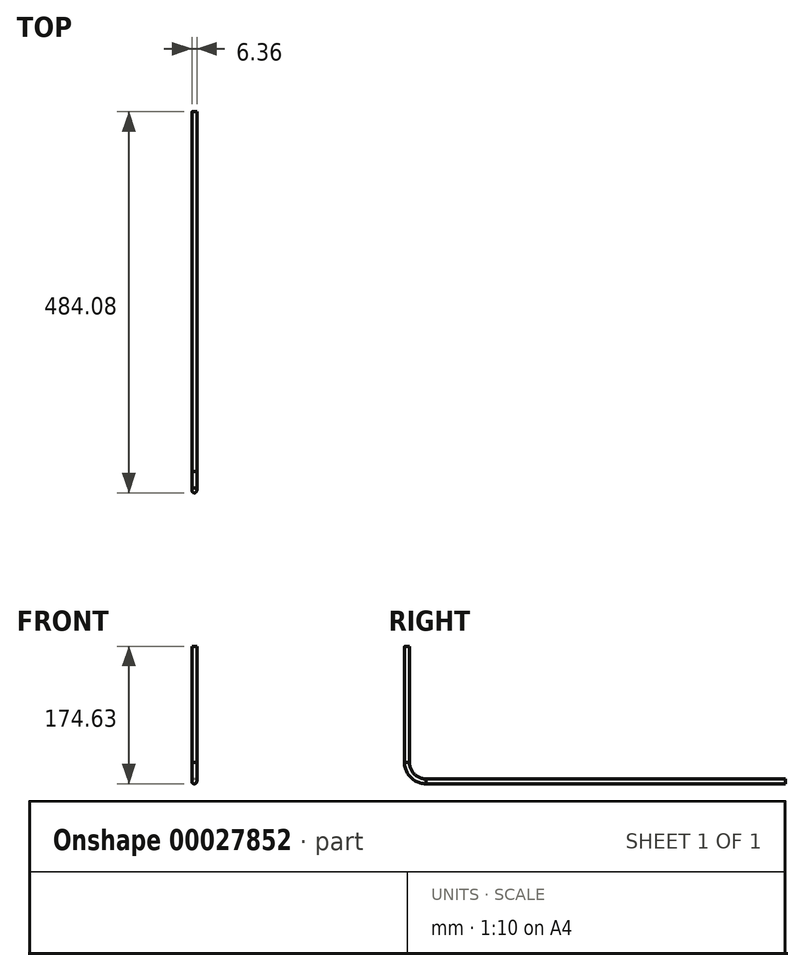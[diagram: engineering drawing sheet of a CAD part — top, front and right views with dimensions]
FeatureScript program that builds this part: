
annotation { "Feature Type Name" : "Feature", "Feature Type Description" : "" }
export const myFeature = defineFeature(function(context is Context, id is Id, definition is map)
    precondition{}
    {
        {
            var Q0;
            Q0=qCreatedBy(makeId("Top.planeOp"),FACE);
            var sketch = newSketch(context, id + "F0", { "sketchPlane" : qUnion([Q0])});
            skCircle(sketch, "E0", {"center": v(0, 0) * mm, "radius": 3.18 * mm});
            skSolve(sketch);
        }
        {
            var Q0;
            Q0=qCreatedBy(makeId("Top.planeOp"),FACE);
            cPlane(context, id + "F1", {"entities" : qUnion([Q0]), "cplaneType" : CPlaneType.OFFSET, "offset" : 147.57 * mm, "oppositeDirection" : true, "width" : 152.4 * mm, "height" : 152.4 * mm});
        }
        {
            var Q0;
            Q0=qCreatedBy(id+"F1.planeOp",FACE);
            var sketch = newSketch(context, id + "F2", { "sketchPlane" : qUnion([Q0])});
            skCircle(sketch, "E1", {"center": v(0, 0) * mm, "radius": 3.18 * mm});
            skSolve(sketch);
        }
        {
            var Q0;
            Q0 = qSketchRegion(id + "F0", true);
            var Q1;
            Q1 = qSketchRegion(id + "F2", true);
            loft(context, id + "F3", {"sheetProfilesArray" : [{ "sheetProfileEntities" : qUnion([Q0]) }, { "sheetProfileEntities" : qUnion([Q1]) }]});
        }
        {
            var Q0;
            Q0=qCreatedBy(makeId("Front.planeOp"),FACE);
            cPlane(context, id + "F4", {"entities" : qUnion([Q0]), "cplaneType" : CPlaneType.OFFSET, "offset" : 23.88 * mm, "oppositeDirection" : true, "width" : 152.4 * mm, "height" : 152.4 * mm});
        }
        {
            var Q0;
            Q0=qCreatedBy(makeId("Right.planeOp"),FACE);
            var sketch = newSketch(context, id + "F5", { "sketchPlane" : qUnion([Q0])});
            skLineSegment(sketch, "E2", {"start": v(0, 0) * mm, "end": v(0, -147.57) * mm});
            skLineSegment(sketch, "E3", {"start": v(0, -147.57) * mm, "end": v(23.88, -147.57) * mm});
            skArc(sketch, "E4", {"start": v(0, -147.57) * mm, "mid": v(7.06, -164.53) * mm, "end": v(24.08, -171.45) * mm});
            skLineSegment(sketch, "E5", {"start": v(23.68, -171.45) * mm, "end": v(480.88, -171.45) * mm});
            skSolve(sketch);
        }
        {
            var Q0;
            Q0 = qSketchRegion(id + "F2", true);
            var Q1;
            Q1=sQuery(id+"F5.wireOp",EDGE,"E4");
            sweep(context, id + "F6", {"profiles" : qUnion([Q0]), "path" : qUnion([Q1])});
        }
        {
            var Q0;
            Q0=makeQuery(id+"F6.opSweep","CAP_FACE",FACE,{"disambiguationData":[OSD([sQuery(id+"F2.wireOp",EDGE,"E1"),sQuery(id+"F5.wireOp",VERTEX,"E4.end")])],"isStart":false});
            var Q1;
            Q1=sQuery(id+"F5.wireOp",EDGE,"E5");
            sweep(context, id + "F7", {"operationType" : NewBodyOperationType.ADD, "profiles" : qUnion([Q0]), "path" : qUnion([Q1])});
        }
    });
